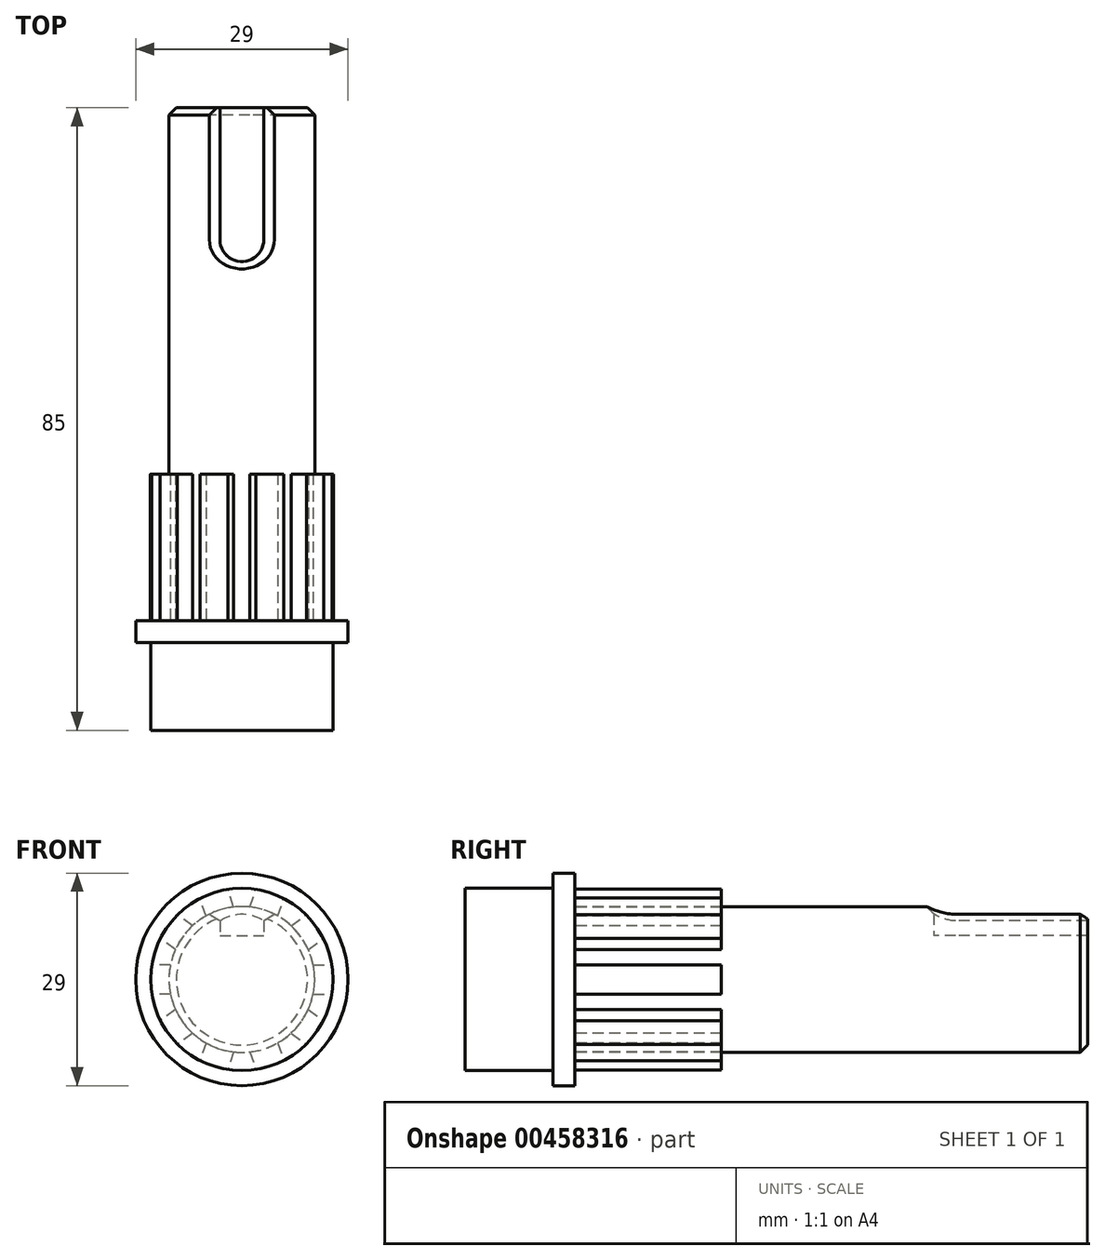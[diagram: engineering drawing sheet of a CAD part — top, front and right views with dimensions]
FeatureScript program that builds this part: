
annotation { "Feature Type Name" : "Feature", "Feature Type Description" : "" }
export const myFeature = defineFeature(function(context is Context, id is Id, definition is map)
    precondition{}
    {
        {
            var Q0;
            Q0=qCreatedBy(makeId("Front.planeOp"),FACE);
            var sketch = newSketch(context, id + "F0", { "sketchPlane" : qUnion([Q0])});
            skCircle(sketch, "E0", {"center": v(0, 0) * mm, "radius": 14.5 * mm});
            skSolve(sketch);
        }
        {
            var Q0;
            Q0 = qSketchRegion(id + "F0", true);
            extrude(context, id + "F1", {"entities" : qUnion([Q0]), "oppositeDirection" : true, "depth" : 3 * mm});
        }
        {
            var Q0;
            Q0=makeQuery(id+"F1.opExtrude","CAP_FACE",FACE,{"disambiguationData":[OSD([sQuery(id+"F0.wireOp",EDGE,"E0")])],"isStart":true});
            var sketch = newSketch(context, id + "F2", { "sketchPlane" : qUnion([Q0])});
            skCircle(sketch, "E1", {"center": v(0, 0) * mm, "radius": 12.45 * mm});
            skSolve(sketch);
        }
        {
            var Q0;
            Q0 = qSketchRegion(id + "F2", true);
            extrude(context, id + "F3", {"entities" : qUnion([Q0]), "operationType" : NewBodyOperationType.ADD, "depth" : 12 * mm});
        }
        {
            var Q0;
            Q0=makeQuery(id+"F1.opExtrude","CAP_FACE",FACE,{"disambiguationData":[OSD([sQuery(id+"F0.wireOp",EDGE,"E0")])],"isStart":false});
            var sketch = newSketch(context, id + "F4", { "sketchPlane" : qUnion([Q0])});
            skCircle(sketch, "E2", {"center": v(0, 0) * mm, "radius": 12.5 * mm});
            skCircle(sketch, "E3", {"center": v(0, 0) * mm, "radius": 9.95 * mm});
            skLineSegment(sketch, "E4", {"start": v(0, 0) * mm, "end": v(18.82, 0) * mm, "construction": true});
            skLineSegment(sketch, "E5", {"start": v(9.75, 2) * mm, "end": v(12.34, 2) * mm});
            skLineSegment(sketch, "E6.MirrorCS", {"start": v(9.75, -2) * mm, "end": v(12.34, -2) * mm});
            skSolve(sketch);
        }
        {
            var Q0;
            Q0=qCreatedBy(makeId("Right.planeOp"),FACE);
            var sketch = newSketch(context, id + "F5", { "sketchPlane" : qUnion([Q0])});
            skLineSegment(sketch, "E7", {"start": v(0, 0) * mm, "end": v(20.44, 0) * mm, "construction": true});
            skSolve(sketch);
        }
        {
            var Q0;
            {var subQ0=sQuery(id+"F4.wireOp",EDGE,"E5");Q0=makeQuery(id+"F4.imprint","IMPRINT",FACE,{"disambiguationData":[TD([[makeQuery(id+"F4.imprint","IMPRINT",EDGE,{"derivedFrom":subQ0}),-1.0]])]});}
            extrude(context, id + "F6", {"entities" : qUnion([Q0]), "operationType" : NewBodyOperationType.ADD, "depth" : 20 * mm});
        }
        {
            var Q0;
            Q0=makeQuery(id+"F1.opExtrude","SWEPT_BODY",BODY,{"disambiguationData":[OSD([sQuery(id+"F0.wireOp",EDGE,"E0")])]});
            var Q1;
            Q1=sQuery(id+"F5.wireOp",EDGE,"E7");
            circularPattern(context, id + "F7", {"entities" : qUnion([Q0]), "axis" : qUnion([Q1]), "angle" : 360 * degree, "instanceCount" : 10, "equalSpace" : true});
        }
        {
            var Q0;
            Q0=makeQuery(id+"F7.opPattern","COPY",FACE,{"derivedFrom":makeQuery(id+"F1.opExtrude","CAP_FACE",FACE,{"disambiguationData":[OSD([sQuery(id+"F0.wireOp",EDGE,"E0")])],"isStart":false}),"instanceName":"3"});
            var sketch = newSketch(context, id + "F8", { "sketchPlane" : qUnion([Q0])});
            skCircle(sketch, "E8", {"center": v(0, 0) * mm, "radius": 9.95 * mm});
            skSolve(sketch);
        }
        {
            var Q0;
            {var subQ0=sQuery(id+"F8.wireOp",EDGE,"E8");var subQ1=makeQuery(id+"F8.imprint","INTERSECT",VERTEX,{"derivedFrom":[makeQuery(id+"F7.opPattern","COPY",EDGE,{"derivedFrom":makeQuery(id+"F6.opExtrude","CAP_EDGE",EDGE,{"disambiguationData":[OSD([sQuery(id+"F4.wireOp",EDGE,"E5")])],"isStart":true}),"instanceName":"3"}),subQ0]});Q0=makeQuery(id+"F8.imprint","IMPRINT",FACE,{"disambiguationData":[TD([[makeQuery(id+"F8.imprint","IMPRINT",EDGE,{"disambiguationData":[TD([[subQ1,-1.0]])],"derivedFrom":subQ0}),1.0]])]});}
            extrude(context, id + "F9", {"entities" : qUnion([Q0]), "operationType" : NewBodyOperationType.ADD, "depth" : 20 * mm});
        }
        {
            var Q0;
            Q0=makeQuery(id+"F9.opExtrude","CAP_FACE",FACE,{"disambiguationData":[OSD([sQuery(id+"F8.wireOp",EDGE,"E8")])],"isStart":false});
            var sketch = newSketch(context, id + "F10", { "sketchPlane" : qUnion([Q0])});
            skCircle(sketch, "E9", {"center": v(0, 0) * mm, "radius": 9.95 * mm});
            skSolve(sketch);
        }
        {
            var Q0;
            Q0 = qSketchRegion(id + "F10", true);
            extrude(context, id + "F11", {"entities" : qUnion([Q0]), "operationType" : NewBodyOperationType.ADD, "depth" : 50 * mm});
        }
        {
            var Q0;
            Q0=qCreatedBy(makeId("Top.planeOp"),FACE);
            cPlane(context, id + "F12", {"entities" : qUnion([Q0]), "cplaneType" : CPlaneType.OFFSET, "offset" : 6 * mm, "width" : 150 * mm, "height" : 150 * mm});
        }
        {
            var Q0;
            Q0=qCreatedBy(id+"F12.planeOp",FACE);
            var sketch = newSketch(context, id + "F13", { "sketchPlane" : qUnion([Q0])});
            skLineSegment(sketch, "E10.bottom", {"start": v(-3, 73) * mm, "end": v(3, 73) * mm});
            skLineSegment(sketch, "E10.top", {"start": v(0, 52) * mm, "end": v(0, 52) * mm});
            skLineSegment(sketch, "E10.left", {"start": v(-3, 73) * mm, "end": v(-3, 55) * mm});
            skLineSegment(sketch, "E10.right", {"start": v(3, 73) * mm, "end": v(3, 55) * mm});
            skPoint(sketch, "E11.firstSnap0", {"position": v(0, 73) * mm});
            skPoint(sketch, "E12.visualSharp", {"position": v(3, 52) * mm});
            skArc(sketch, "E12.filletArc", {"start": v(0, 52) * mm, "mid": v(2.12, 52.88) * mm, "end": v(3, 55) * mm});
            skPoint(sketch, "E13.visualSharp", {"position": v(-3, 52) * mm});
            skArc(sketch, "E13.filletArc", {"start": v(-3, 55) * mm, "mid": v(-2.12, 52.88) * mm, "end": v(0, 52) * mm});
            skSolve(sketch);
        }
        {
            var Q0;
            Q0 = qSketchRegion(id + "F13", true);
            extrude(context, id + "F14", {"entities" : qUnion([Q0]), "operationType" : NewBodyOperationType.REMOVE, "depth" : 3.95 * mm, "offsetDistance" : 25 * mm});
        }
        {
            var Q0;
            {var subQ0=sQuery(id+"F4.wireOp",EDGE,"E6.MirrorCS");var subQ1=sQuery(id+"F4.wireOp",EDGE,"E5");var subQ4=sQuery(id+"F8.wireOp",EDGE,"E8");var subQ7=makeQuery(id+"F6.opExtrude","SWEPT_FACE",FACE,{"disambiguationData":[OSD([subQ0])]});var subQ15=makeQuery(id+"F6.opExtrude","SWEPT_FACE",FACE,{"disambiguationData":[OSD([subQ1])]});var subQ17=makeQuery(id+"F9.opExtrude","SWEPT_FACE",FACE,{"disambiguationData":[OSD([subQ4])]});Q0=makeQuery(id+"F14.boolean.opBoolean","INTERSECT",EDGE,{"derivedFrom":[makeQuery(id+"F11.boolean.opBoolean","MERGE",FACE,{"derivedFrom":[makeQuery(id+"F9.boolean.opBoolean","SPLIT",FACE,{"disambiguationData":[TD([subQ15])],"derivedFrom":subQ17}),makeQuery(id+"F9.boolean.opBoolean","SPLIT",FACE,{"disambiguationData":[TD([subQ7])],"derivedFrom":subQ17}),makeQuery(id+"F9.boolean.opBoolean","SPLIT",FACE,{"disambiguationData":[TD([makeQuery(id+"F7.opPattern","COPY",FACE,{"derivedFrom":subQ15,"instanceName":"1"})])],"derivedFrom":subQ17}),makeQuery(id+"F9.boolean.opBoolean","SPLIT",FACE,{"disambiguationData":[TD([makeQuery(id+"F7.opPattern","COPY",FACE,{"derivedFrom":subQ15,"instanceName":"2"})])],"derivedFrom":subQ17}),makeQuery(id+"F9.boolean.opBoolean","SPLIT",FACE,{"disambiguationData":[TD([makeQuery(id+"F7.opPattern","COPY",FACE,{"derivedFrom":subQ15,"instanceName":"3"})])],"derivedFrom":subQ17}),makeQuery(id+"F9.boolean.opBoolean","SPLIT",FACE,{"disambiguationData":[TD([makeQuery(id+"F7.opPattern","COPY",FACE,{"derivedFrom":subQ15,"instanceName":"4"})])],"derivedFrom":subQ17}),makeQuery(id+"F9.boolean.opBoolean","SPLIT",FACE,{"disambiguationData":[TD([makeQuery(id+"F7.opPattern","COPY",FACE,{"derivedFrom":subQ15,"instanceName":"5"})])],"derivedFrom":subQ17}),makeQuery(id+"F9.boolean.opBoolean","SPLIT",FACE,{"disambiguationData":[TD([makeQuery(id+"F7.opPattern","COPY",FACE,{"derivedFrom":subQ15,"instanceName":"6"})])],"derivedFrom":subQ17}),makeQuery(id+"F9.boolean.opBoolean","SPLIT",FACE,{"disambiguationData":[TD([makeQuery(id+"F7.opPattern","COPY",FACE,{"derivedFrom":subQ15,"instanceName":"7"})])],"derivedFrom":subQ17}),makeQuery(id+"F9.boolean.opBoolean","SPLIT",FACE,{"disambiguationData":[TD([makeQuery(id+"F7.opPattern","COPY",FACE,{"derivedFrom":subQ15,"instanceName":"8"})])],"derivedFrom":subQ17}),makeQuery(id+"F11.opExtrude","SWEPT_FACE",FACE,{"disambiguationData":[OSD([sQuery(id+"F10.wireOp",EDGE,"E9")])]})]}),makeQuery(id+"F14.opExtrude","SWEPT_FACE",FACE,{"disambiguationData":[OSD([sQuery(id+"F13.wireOp",EDGE,"E10.right")])]})]});}
            var Q1;
            {var subQ0=sQuery(id+"F4.wireOp",EDGE,"E6.MirrorCS");var subQ1=sQuery(id+"F4.wireOp",EDGE,"E5");var subQ4=sQuery(id+"F8.wireOp",EDGE,"E8");var subQ7=makeQuery(id+"F6.opExtrude","SWEPT_FACE",FACE,{"disambiguationData":[OSD([subQ0])]});var subQ15=makeQuery(id+"F6.opExtrude","SWEPT_FACE",FACE,{"disambiguationData":[OSD([subQ1])]});var subQ17=makeQuery(id+"F9.opExtrude","SWEPT_FACE",FACE,{"disambiguationData":[OSD([subQ4])]});Q1=makeQuery(id+"F14.boolean.opBoolean","INTERSECT",EDGE,{"derivedFrom":[makeQuery(id+"F11.boolean.opBoolean","MERGE",FACE,{"derivedFrom":[makeQuery(id+"F9.boolean.opBoolean","SPLIT",FACE,{"disambiguationData":[TD([subQ15])],"derivedFrom":subQ17}),makeQuery(id+"F9.boolean.opBoolean","SPLIT",FACE,{"disambiguationData":[TD([subQ7])],"derivedFrom":subQ17}),makeQuery(id+"F9.boolean.opBoolean","SPLIT",FACE,{"disambiguationData":[TD([makeQuery(id+"F7.opPattern","COPY",FACE,{"derivedFrom":subQ15,"instanceName":"1"})])],"derivedFrom":subQ17}),makeQuery(id+"F9.boolean.opBoolean","SPLIT",FACE,{"disambiguationData":[TD([makeQuery(id+"F7.opPattern","COPY",FACE,{"derivedFrom":subQ15,"instanceName":"2"})])],"derivedFrom":subQ17}),makeQuery(id+"F9.boolean.opBoolean","SPLIT",FACE,{"disambiguationData":[TD([makeQuery(id+"F7.opPattern","COPY",FACE,{"derivedFrom":subQ15,"instanceName":"3"})])],"derivedFrom":subQ17}),makeQuery(id+"F9.boolean.opBoolean","SPLIT",FACE,{"disambiguationData":[TD([makeQuery(id+"F7.opPattern","COPY",FACE,{"derivedFrom":subQ15,"instanceName":"4"})])],"derivedFrom":subQ17}),makeQuery(id+"F9.boolean.opBoolean","SPLIT",FACE,{"disambiguationData":[TD([makeQuery(id+"F7.opPattern","COPY",FACE,{"derivedFrom":subQ15,"instanceName":"5"})])],"derivedFrom":subQ17}),makeQuery(id+"F9.boolean.opBoolean","SPLIT",FACE,{"disambiguationData":[TD([makeQuery(id+"F7.opPattern","COPY",FACE,{"derivedFrom":subQ15,"instanceName":"6"})])],"derivedFrom":subQ17}),makeQuery(id+"F9.boolean.opBoolean","SPLIT",FACE,{"disambiguationData":[TD([makeQuery(id+"F7.opPattern","COPY",FACE,{"derivedFrom":subQ15,"instanceName":"7"})])],"derivedFrom":subQ17}),makeQuery(id+"F9.boolean.opBoolean","SPLIT",FACE,{"disambiguationData":[TD([makeQuery(id+"F7.opPattern","COPY",FACE,{"derivedFrom":subQ15,"instanceName":"8"})])],"derivedFrom":subQ17}),makeQuery(id+"F11.opExtrude","SWEPT_FACE",FACE,{"disambiguationData":[OSD([sQuery(id+"F10.wireOp",EDGE,"E9")])]})]}),makeQuery(id+"F14.opExtrude","SWEPT_FACE",FACE,{"disambiguationData":[OSD([sQuery(id+"F13.wireOp",EDGE,"E12.filletArc"),sQuery(id+"F13.wireOp",EDGE,"E13.filletArc")])]})]});}
            var Q2;
            {var subQ0=sQuery(id+"F4.wireOp",EDGE,"E6.MirrorCS");var subQ1=sQuery(id+"F4.wireOp",EDGE,"E5");var subQ4=sQuery(id+"F8.wireOp",EDGE,"E8");var subQ7=makeQuery(id+"F6.opExtrude","SWEPT_FACE",FACE,{"disambiguationData":[OSD([subQ0])]});var subQ15=makeQuery(id+"F6.opExtrude","SWEPT_FACE",FACE,{"disambiguationData":[OSD([subQ1])]});var subQ17=makeQuery(id+"F9.opExtrude","SWEPT_FACE",FACE,{"disambiguationData":[OSD([subQ4])]});Q2=makeQuery(id+"F14.boolean.opBoolean","INTERSECT",EDGE,{"derivedFrom":[makeQuery(id+"F11.boolean.opBoolean","MERGE",FACE,{"derivedFrom":[makeQuery(id+"F9.boolean.opBoolean","SPLIT",FACE,{"disambiguationData":[TD([subQ15])],"derivedFrom":subQ17}),makeQuery(id+"F9.boolean.opBoolean","SPLIT",FACE,{"disambiguationData":[TD([subQ7])],"derivedFrom":subQ17}),makeQuery(id+"F9.boolean.opBoolean","SPLIT",FACE,{"disambiguationData":[TD([makeQuery(id+"F7.opPattern","COPY",FACE,{"derivedFrom":subQ15,"instanceName":"1"})])],"derivedFrom":subQ17}),makeQuery(id+"F9.boolean.opBoolean","SPLIT",FACE,{"disambiguationData":[TD([makeQuery(id+"F7.opPattern","COPY",FACE,{"derivedFrom":subQ15,"instanceName":"2"})])],"derivedFrom":subQ17}),makeQuery(id+"F9.boolean.opBoolean","SPLIT",FACE,{"disambiguationData":[TD([makeQuery(id+"F7.opPattern","COPY",FACE,{"derivedFrom":subQ15,"instanceName":"3"})])],"derivedFrom":subQ17}),makeQuery(id+"F9.boolean.opBoolean","SPLIT",FACE,{"disambiguationData":[TD([makeQuery(id+"F7.opPattern","COPY",FACE,{"derivedFrom":subQ15,"instanceName":"4"})])],"derivedFrom":subQ17}),makeQuery(id+"F9.boolean.opBoolean","SPLIT",FACE,{"disambiguationData":[TD([makeQuery(id+"F7.opPattern","COPY",FACE,{"derivedFrom":subQ15,"instanceName":"5"})])],"derivedFrom":subQ17}),makeQuery(id+"F9.boolean.opBoolean","SPLIT",FACE,{"disambiguationData":[TD([makeQuery(id+"F7.opPattern","COPY",FACE,{"derivedFrom":subQ15,"instanceName":"6"})])],"derivedFrom":subQ17}),makeQuery(id+"F9.boolean.opBoolean","SPLIT",FACE,{"disambiguationData":[TD([makeQuery(id+"F7.opPattern","COPY",FACE,{"derivedFrom":subQ15,"instanceName":"7"})])],"derivedFrom":subQ17}),makeQuery(id+"F9.boolean.opBoolean","SPLIT",FACE,{"disambiguationData":[TD([makeQuery(id+"F7.opPattern","COPY",FACE,{"derivedFrom":subQ15,"instanceName":"8"})])],"derivedFrom":subQ17}),makeQuery(id+"F11.opExtrude","SWEPT_FACE",FACE,{"disambiguationData":[OSD([sQuery(id+"F10.wireOp",EDGE,"E9")])]})]}),makeQuery(id+"F14.opExtrude","SWEPT_FACE",FACE,{"disambiguationData":[OSD([sQuery(id+"F13.wireOp",EDGE,"E10.left")])]})]});}
            var Q3;
            Q3=makeQuery(id+"F11.opExtrude","CAP_EDGE",EDGE,{"disambiguationData":[OSD([sQuery(id+"F10.wireOp",EDGE,"E9")])],"isStart":false});
            chamfer(context, id + "F15", {"entities" : qUnion([Q0, Q1, Q2, Q3]), "width" : 1 * mm, "tangentPropagation" : true});
        }
    });
